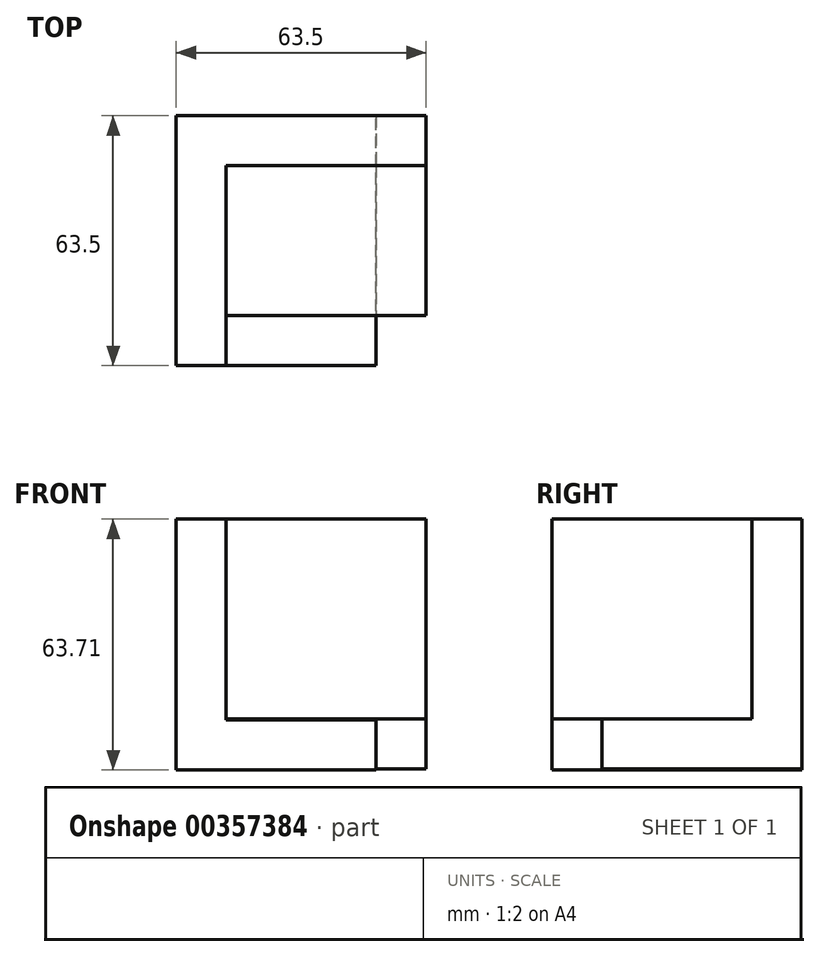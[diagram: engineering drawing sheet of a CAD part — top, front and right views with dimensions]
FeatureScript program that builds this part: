
annotation { "Feature Type Name" : "Feature", "Feature Type Description" : "" }
export const myFeature = defineFeature(function(context is Context, id is Id, definition is map)
    precondition{}
    {
        {
            var Q0;
            Q0=qCreatedBy(makeId("Front.planeOp"),FACE);
            var sketch = newSketch(context, id + "F0", { "sketchPlane" : qUnion([Q0])});
            skLineSegment(sketch, "E0.bottom", {"start": v(0, 0) * mm, "end": v(63.5, 0) * mm});
            skLineSegment(sketch, "E0.top", {"start": v(0, -63.5) * mm, "end": v(63.5, -63.5) * mm});
            skLineSegment(sketch, "E0.left", {"start": v(0, 0) * mm, "end": v(0, -63.5) * mm});
            skLineSegment(sketch, "E0.right", {"start": v(63.5, 0) * mm, "end": v(63.5, -63.5) * mm});
            skSolve(sketch);
        }
        {
            var Q0;
            Q0 = qSketchRegion(id + "F0", true);
            extrude(context, id + "F1", {"entities" : qUnion([Q0]), "depth" : 12.7 * mm});
        }
        {
            var Q0;
            Q0=qCreatedBy(makeId("Right.planeOp"),FACE);
            var sketch = newSketch(context, id + "F2", { "sketchPlane" : qUnion([Q0])});
            skLineSegment(sketch, "E1.bottom", {"start": v(0, 0) * mm, "end": v(-63.5, 0) * mm});
            skLineSegment(sketch, "E1.top", {"start": v(0, -63.5) * mm, "end": v(-63.5, -63.5) * mm});
            skLineSegment(sketch, "E1.left", {"start": v(0, 0) * mm, "end": v(0, -63.5) * mm});
            skLineSegment(sketch, "E1.right", {"start": v(-63.5, 0) * mm, "end": v(-63.5, -63.5) * mm});
            skSolve(sketch);
        }
        {
            var Q0;
            Q0 = qSketchRegion(id + "F2", true);
            extrude(context, id + "F3", {"entities" : qUnion([Q0]), "operationType" : NewBodyOperationType.ADD, "depth" : 12.7 * mm});
        }
        {
            var Q0;
            Q0=qCreatedBy(makeId("Front.planeOp"),FACE);
            var sketch = newSketch(context, id + "F4", { "sketchPlane" : qUnion([Q0])});
            skLineSegment(sketch, "E2.bottom", {"start": v(0, -63.5) * mm, "end": v(63.5, -63.5) * mm});
            skLineSegment(sketch, "E2.top", {"start": v(0, -50.8) * mm, "end": v(63.5, -50.8) * mm});
            skLineSegment(sketch, "E2.left", {"start": v(0, -63.5) * mm, "end": v(0, -50.8) * mm});
            skLineSegment(sketch, "E2.right", {"start": v(63.5, -63.5) * mm, "end": v(63.5, -50.8) * mm});
            skSolve(sketch);
        }
        {
            var Q0;
            Q0 = qSketchRegion(id + "F4", true);
            extrude(context, id + "F5", {"entities" : qUnion([Q0]), "operationType" : NewBodyOperationType.ADD, "depth" : 50.8 * mm});
        }
        {
            var Q0;
            Q0=qCreatedBy(makeId("Right.planeOp"),FACE);
            var sketch = newSketch(context, id + "F6", { "sketchPlane" : qUnion([Q0])});
            skLineSegment(sketch, "E3.bottom", {"start": v(-63.47, -63.46) * mm, "end": v(-50.77, -63.46) * mm});
            skLineSegment(sketch, "E3.top", {"start": v(-63.47, -50.76) * mm, "end": v(-50.77, -50.76) * mm});
            skLineSegment(sketch, "E3.left", {"start": v(-63.47, -63.46) * mm, "end": v(-63.47, -50.76) * mm});
            skLineSegment(sketch, "E3.right", {"start": v(-50.77, -63.46) * mm, "end": v(-50.77, -50.76) * mm});
            skSolve(sketch);
        }
        {
            var Q0;
            Q0 = qSketchRegion(id + "F6", true);
            extrude(context, id + "F7", {"entities" : qUnion([Q0]), "operationType" : NewBodyOperationType.ADD, "depth" : 50.8 * mm});
        }
        {
            var Q0;
            Q0=qCreatedBy(makeId("Front.planeOp"),FACE);
            var sketch = newSketch(context, id + "F8", { "sketchPlane" : qUnion([Q0])});
            skLineSegment(sketch, "E4.bottom", {"start": v(0, -63.7) * mm, "end": v(50.8, -63.7) * mm});
            skLineSegment(sketch, "E4.top", {"start": v(0, -51) * mm, "end": v(50.8, -51) * mm});
            skLineSegment(sketch, "E4.left", {"start": v(0, -63.7) * mm, "end": v(0, -51) * mm});
            skLineSegment(sketch, "E4.right", {"start": v(50.8, -63.7) * mm, "end": v(50.8, -51) * mm});
            skSolve(sketch);
        }
        {
            var Q0;
            Q0 = qSketchRegion(id + "F8", true);
            extrude(context, id + "F9", {"entities" : qUnion([Q0]), "operationType" : NewBodyOperationType.ADD, "depth" : 63.5 * mm});
        }
    });
